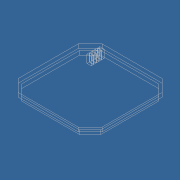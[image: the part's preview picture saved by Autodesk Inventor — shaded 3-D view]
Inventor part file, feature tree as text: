
AUTODESK INVENTOR PART (.ipt)
format: ipt  version: unknown  size: 1,184,768 bytes
history: native  units: mm
features: extrude x3, sketch x3, other x1
ambient origin geometry x8: Origin, YZ Plane, XZ Plane, XY Plane, X Axis, Y Axis, Z Axis, Center Point
feature tree (7):
  extrude  "Estrusione10"  Depth=59.0mm
  extrude  "Estrusione11"  Depth=59.0mm
  extrude  "Estrusione12"  Depth=8.0mm
  sketch  "Schizzo1"
  sketch  "Schizzo12"
  sketch  "Schizzo13"
  other  "Immagine3"
